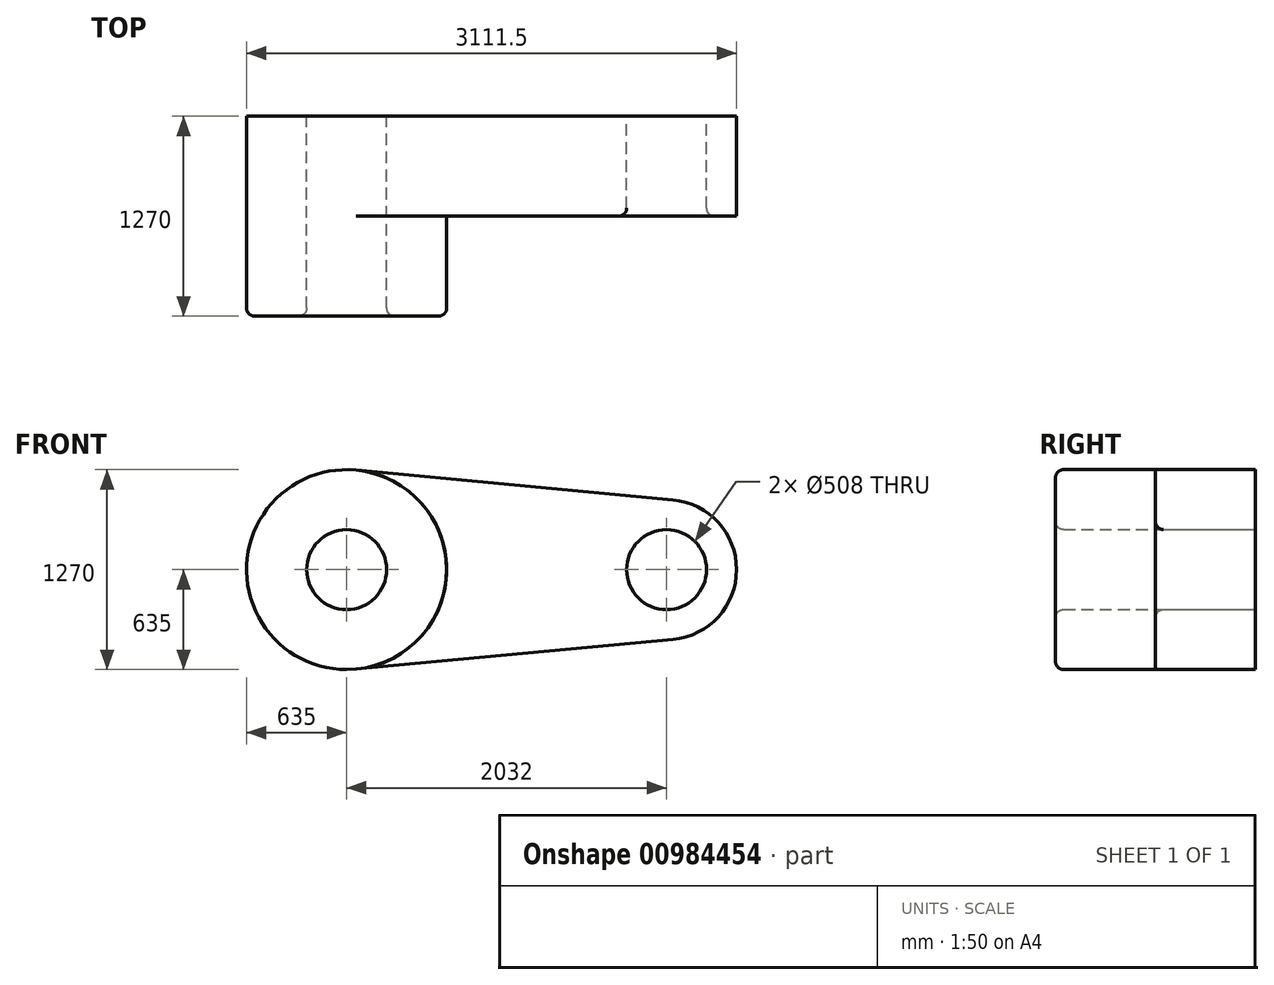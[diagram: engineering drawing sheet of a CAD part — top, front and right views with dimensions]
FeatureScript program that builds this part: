
annotation { "Feature Type Name" : "Feature", "Feature Type Description" : "" }
export const myFeature = defineFeature(function(context is Context, id is Id, definition is map)
    precondition{}
    {
        {
            var Q0;
            Q0=qCreatedBy(makeId("Front.planeOp"),FACE);
            var sketch = newSketch(context, id + "F0", { "sketchPlane" : qUnion([Q0])});
            skCircle(sketch, "E0", {"center": v(0, 0) * mm, "radius": 635 * mm});
            skCircle(sketch, "E1", {"center": v(2032, 0) * mm, "radius": 444.5 * mm});
            skLineSegment(sketch, "E2", {"start": v(59.53, 632.2) * mm, "end": v(2073.67, 442.54) * mm});
            skLineSegment(sketch, "E3", {"start": v(59.53, -632.2) * mm, "end": v(2073.67, -442.54) * mm});
            skLineSegment(sketch, "E4", {"start": v(1066.6, -94.83) * mm, "end": v(1066.6, -94.83) * mm});
            skCircle(sketch, "E5", {"center": v(0, 0) * mm, "radius": 254 * mm});
            skCircle(sketch, "E6", {"center": v(2032, 0) * mm, "radius": 254 * mm});
            skSolve(sketch);
        }
        {
            var Q0;
            Q0 = qSketchRegion(id + "F0", true);
            extrude(context, id + "F1", {"entities" : qUnion([Q0]), "depth" : 635 * mm, "offsetDistance" : 25.4 * mm});
        }
        {
            var Q0;
            Q0=makeQuery(id+"F0.imprint","IMPRINT",FACE,{"disambiguationData":[TD([[makeQuery(id+"F0.imprint","IMPRINT",EDGE,{"derivedFrom":sQuery(id+"F0.wireOp",EDGE,"E5")}),-1.0]])]});
            extrude(context, id + "F2", {"entities" : qUnion([Q0]), "operationType" : NewBodyOperationType.ADD, "depth" : 1270 * mm, "offsetDistance" : 25.4 * mm});
        }
        {
            var Q0;
            Q0=makeQuery(id+"F2.opExtrude","CAP_EDGE",EDGE,{"disambiguationData":[OSD([sQuery(id+"F0.wireOp",EDGE,"E5")])],"isStart":false});
            var Q1;
            Q1=makeQuery(id+"F2.opExtrude","CAP_EDGE",EDGE,{"disambiguationData":[OSD([sQuery(id+"F0.wireOp",EDGE,"E0")])],"isStart":false});
            var Q2;
            Q2=makeQuery(id+"F1.opExtrude","CAP_EDGE",EDGE,{"disambiguationData":[OSD([sQuery(id+"F0.wireOp",EDGE,"E6")])],"isStart":false});
            fillet(context, id + "F3", {"entities" : qUnion([Q0, Q1, Q2]), "radius" : 50.8 * mm, "tangentPropagation" : true, "allowEdgeOverflow" : false});
        }
    });
